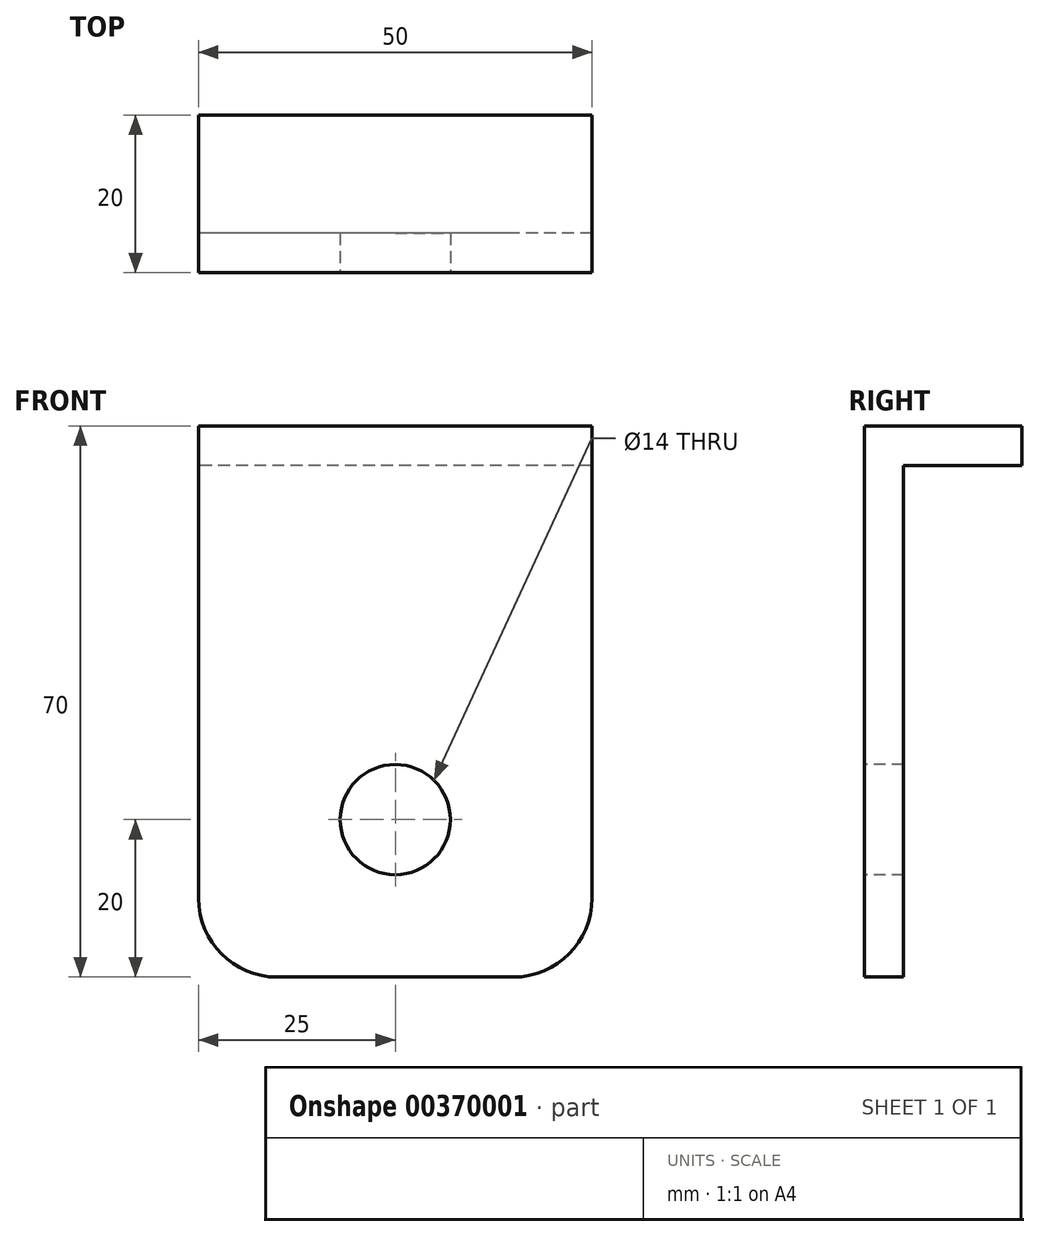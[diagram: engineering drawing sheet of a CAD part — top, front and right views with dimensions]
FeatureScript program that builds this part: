
annotation { "Feature Type Name" : "Feature", "Feature Type Description" : "" }
export const myFeature = defineFeature(function(context is Context, id is Id, definition is map)
    precondition{}
    {
        {
            var Q0;
            Q0=qCreatedBy(makeId("Right.planeOp"),FACE);
            var sketch = newSketch(context, id + "F0", { "sketchPlane" : qUnion([Q0])});
            skLineSegment(sketch, "E0", {"start": v(0, -65) * mm, "end": v(-5, -65) * mm});
            skLineSegment(sketch, "E1", {"start": v(-5, -65) * mm, "end": v(-5, 5) * mm});
            skLineSegment(sketch, "E2", {"start": v(-5, 5) * mm, "end": v(15, 5) * mm});
            skLineSegment(sketch, "E3", {"start": v(15, 5) * mm, "end": v(15, 0) * mm});
            skLineSegment(sketch, "E4", {"start": v(15, 0) * mm, "end": v(0, 0) * mm});
            skLineSegment(sketch, "E5", {"start": v(0, 0) * mm, "end": v(0, -65) * mm});
            skSolve(sketch);
        }
        {
            var Q0;
            Q0 = qSketchRegion(id + "F0", true);
            extrude(context, id + "F1", {"entities" : qUnion([Q0]), "depth" : 50 * mm});
        }
        {
            var Q0;
            Q0=makeQuery(id+"F1.opExtrude","SWEPT_FACE",FACE,{"disambiguationData":[OSD([sQuery(id+"F0.wireOp",EDGE,"E1")])]});
            var sketch = newSketch(context, id + "F2", { "sketchPlane" : qUnion([Q0])});
            skCircle(sketch, "E6", {"center": v(25, -45) * mm, "radius": 7 * mm});
            skSolve(sketch);
        }
        {
            var Q0;
            Q0 = qSketchRegion(id + "F2", true);
            extrude(context, id + "F3", {"entities" : qUnion([Q0]), "operationType" : NewBodyOperationType.REMOVE, "oppositeDirection" : true, "depth" : 25 * mm});
        }
        {
            var Q0;
            Q0=makeQuery(id+"F1.opExtrude","CAP_EDGE",EDGE,{"disambiguationData":[OSD([sQuery(id+"F0.wireOp",EDGE,"E0")])],"isStart":true});
            var Q1;
            Q1=makeQuery(id+"F1.opExtrude","CAP_EDGE",EDGE,{"disambiguationData":[OSD([sQuery(id+"F0.wireOp",EDGE,"E0")])],"isStart":false});
            fillet(context, id + "F4", {"entities" : qUnion([Q0, Q1]), "radius" : 10 * mm, "tangentPropagation" : true, "allowEdgeOverflow" : false});
        }
    });
